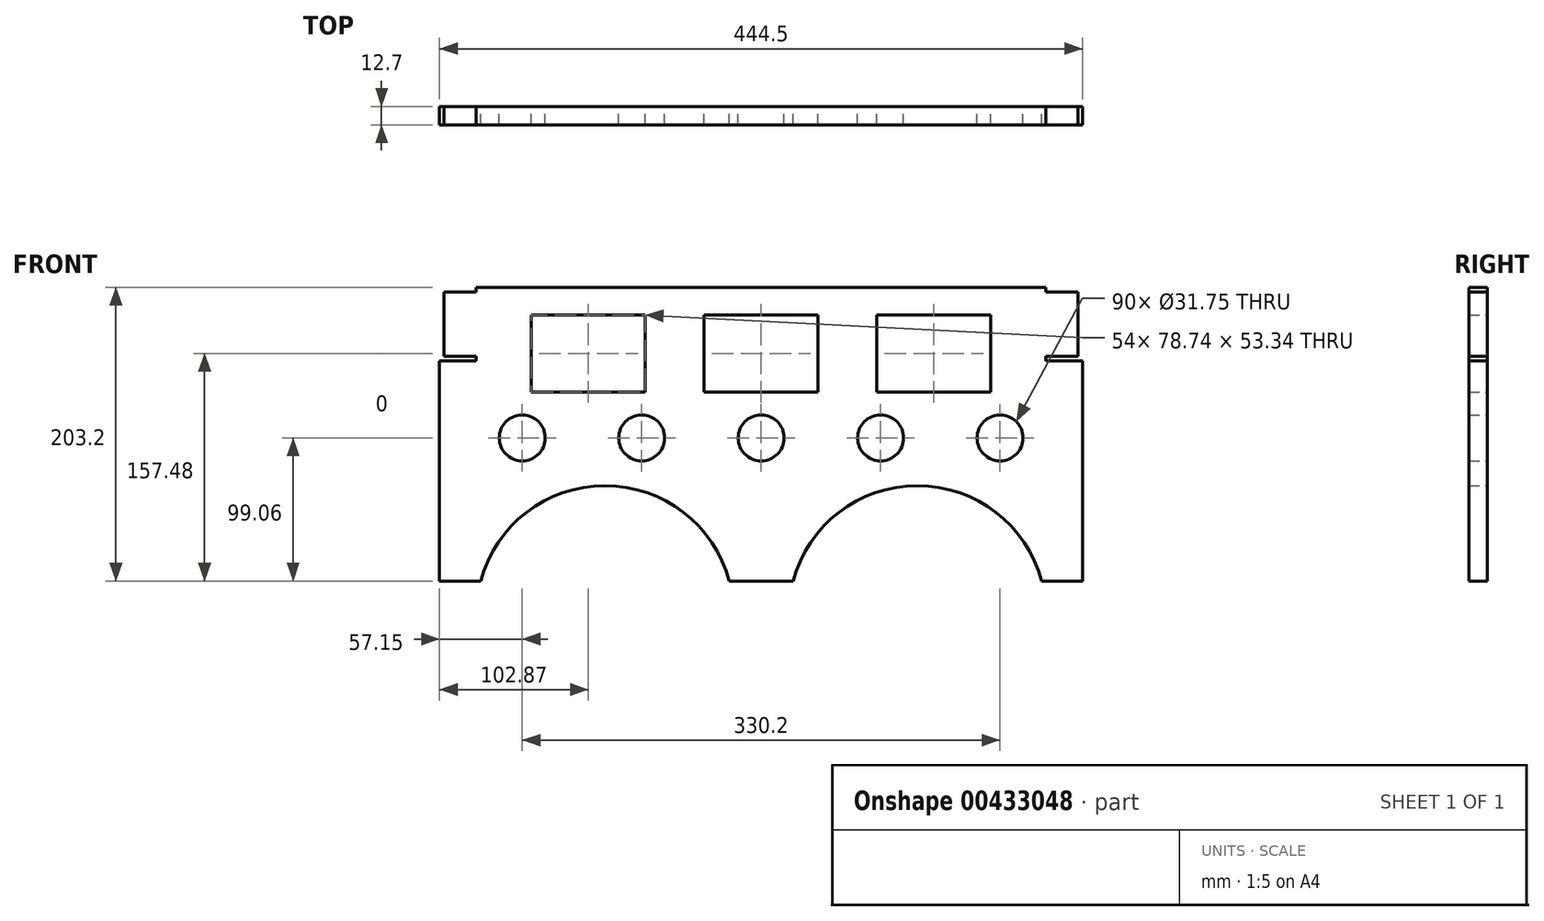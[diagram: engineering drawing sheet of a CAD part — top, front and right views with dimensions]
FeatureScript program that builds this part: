
annotation { "Feature Type Name" : "Feature", "Feature Type Description" : "" }
export const myFeature = defineFeature(function(context is Context, id is Id, definition is map)
    precondition{}
    {
        {
            var Q0;
            Q0=qCreatedBy(makeId("Front.planeOp"),FACE);
            var sketch = newSketch(context, id + "F0", { "sketchPlane" : qUnion([Q0])});
            skLineSegment(sketch, "E0", {"start": v(22.04, 0) * mm, "end": v(-22.04, 0) * mm});
            skLineSegment(sketch, "E1", {"start": v(-193.86, 0) * mm, "end": v(-222.25, 0) * mm});
            skLineSegment(sketch, "E2", {"start": v(-222.25, 0) * mm, "end": v(-222.25, 152.4) * mm});
            skLineSegment(sketch, "E3", {"start": v(-222.25, 152.4) * mm, "end": v(-196.85, 152.4) * mm});
            skLineSegment(sketch, "E4", {"start": v(-196.85, 152.4) * mm, "end": v(-196.85, 155.58) * mm});
            skLineSegment(sketch, "E5", {"start": v(-196.85, 155.58) * mm, "end": v(-219.08, 155.58) * mm});
            skLineSegment(sketch, "E6", {"start": v(-219.08, 155.58) * mm, "end": v(-219.08, 200.03) * mm});
            skLineSegment(sketch, "E7", {"start": v(-219.08, 200.02) * mm, "end": v(-196.85, 200.02) * mm});
            skLineSegment(sketch, "E8", {"start": v(-196.85, 200.03) * mm, "end": v(-196.85, 203.2) * mm});
            skLineSegment(sketch, "E9", {"start": v(-196.85, 203.2) * mm, "end": v(196.85, 203.2) * mm});
            skLineSegment(sketch, "E10", {"start": v(196.85, 203.2) * mm, "end": v(196.85, 200.03) * mm});
            skLineSegment(sketch, "E11", {"start": v(196.85, 200.03) * mm, "end": v(219.08, 200.03) * mm});
            skLineSegment(sketch, "E12", {"start": v(219.07, 200.03) * mm, "end": v(219.07, 155.58) * mm});
            skLineSegment(sketch, "E13", {"start": v(219.08, 155.58) * mm, "end": v(196.85, 155.58) * mm});
            skLineSegment(sketch, "E14", {"start": v(196.85, 155.58) * mm, "end": v(196.85, 152.4) * mm});
            skLineSegment(sketch, "E15", {"start": v(196.85, 152.4) * mm, "end": v(222.25, 152.4) * mm});
            skLineSegment(sketch, "E16", {"start": v(222.25, 152.4) * mm, "end": v(222.25, 0) * mm});
            skLineSegment(sketch, "E17", {"start": v(222.25, 0) * mm, "end": v(193.86, 0) * mm});
            skArc(sketch, "E18", {"start": v(-22.04, 0) * mm, "mid": v(-107.95, 66.04) * mm, "end": v(-193.86, 0) * mm});
            skArc(sketch, "E19", {"start": v(193.86, 0) * mm, "mid": v(107.95, 66.04) * mm, "end": v(22.04, 0) * mm});
            skLineSegment(sketch, "E20.bottom", {"start": v(-158.75, 184.15) * mm, "end": v(-80.01, 184.15) * mm});
            skLineSegment(sketch, "E20.top", {"start": v(-158.75, 130.8) * mm, "end": v(-80.01, 130.8) * mm});
            skLineSegment(sketch, "E20.left", {"start": v(-158.75, 184.15) * mm, "end": v(-158.75, 130.8) * mm});
            skLineSegment(sketch, "E20.right", {"start": v(-80.01, 184.15) * mm, "end": v(-80.01, 130.8) * mm});
            skLineSegment(sketch, "E21.bottom", {"start": v(-39.37, 184.15) * mm, "end": v(39.37, 184.15) * mm});
            skLineSegment(sketch, "E21.top", {"start": v(-39.37, 130.8) * mm, "end": v(39.37, 130.8) * mm});
            skLineSegment(sketch, "E21.left", {"start": v(-39.37, 184.15) * mm, "end": v(-39.37, 130.8) * mm});
            skLineSegment(sketch, "E21.right", {"start": v(39.37, 184.15) * mm, "end": v(39.37, 130.8) * mm});
            skLineSegment(sketch, "E22.bottom", {"start": v(80, 184.15) * mm, "end": v(158.75, 184.15) * mm});
            skLineSegment(sketch, "E22.top", {"start": v(80, 130.81) * mm, "end": v(158.75, 130.81) * mm});
            skLineSegment(sketch, "E22.left", {"start": v(80, 184.15) * mm, "end": v(80, 130.8) * mm});
            skLineSegment(sketch, "E22.right", {"start": v(158.75, 184.15) * mm, "end": v(158.75, 130.81) * mm});
            skCircle(sketch, "E23", {"center": v(-165.1, 99.06) * mm, "radius": 15.88 * mm});
            skCircle(sketch, "E24", {"center": v(0, 99.06) * mm, "radius": 15.88 * mm});
            skCircle(sketch, "E25", {"center": v(-82.55, 99.06) * mm, "radius": 15.88 * mm});
            skCircle(sketch, "E26", {"center": v(82.55, 99.06) * mm, "radius": 15.88 * mm});
            skCircle(sketch, "E27", {"center": v(165.1, 99.06) * mm, "radius": 15.88 * mm});
            skPoint(sketch, "E28.centerSnap0", {"position": v(-207.96, 155.58) * mm});
            skSolve(sketch);
        }
        {
            var Q0;
            Q0=makeQuery(id+"F0.imprint","IMPRINT",FACE,{"disambiguationData":[TD([[makeQuery(id+"F0.imprint","IMPRINT",EDGE,{"derivedFrom":sQuery(id+"F0.wireOp",EDGE,"E0")}),-1.0]])]});
            extrude(context, id + "F1", {"entities" : qUnion([Q0]), "depth" : 12.7 * mm});
        }
    });
